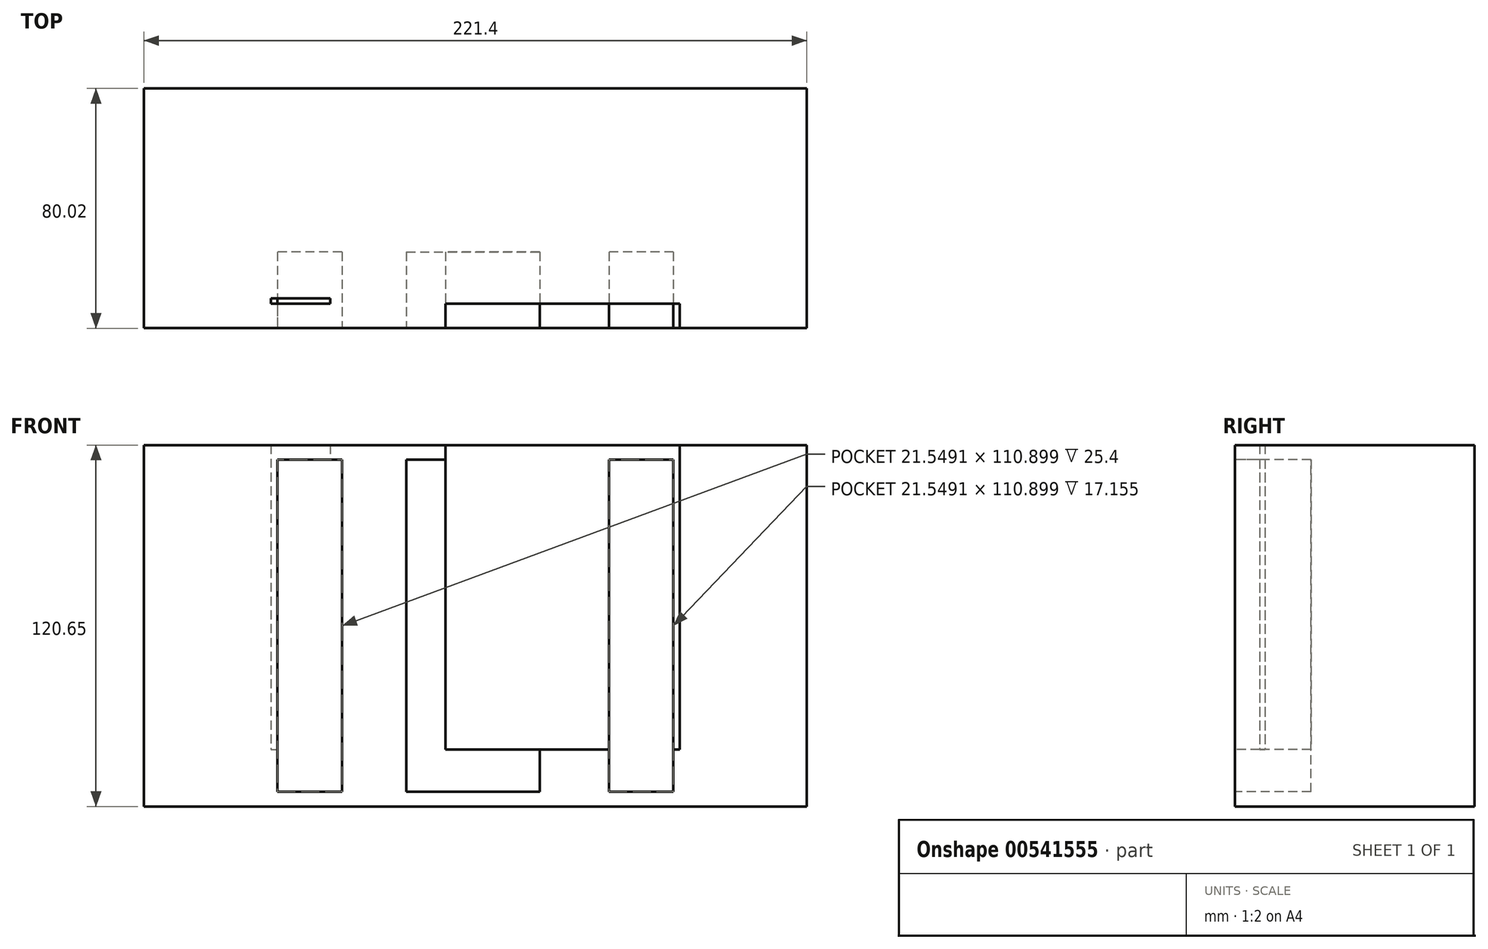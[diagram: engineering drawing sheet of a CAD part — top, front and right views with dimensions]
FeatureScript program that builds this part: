
annotation { "Feature Type Name" : "Feature", "Feature Type Description" : "" }
export const myFeature = defineFeature(function(context is Context, id is Id, definition is map)
    precondition{}
    {
        {
            var Q0;
            Q0=qCreatedBy(makeId("Top.planeOp"),FACE);
            var sketch = newSketch(context, id + "F0", { "sketchPlane" : qUnion([Q0])});
            skLineSegment(sketch, "E0.bottom", {"start": v(110.7, -40) * mm, "end": v(-110.7, -40) * mm});
            skLineSegment(sketch, "E0.top", {"start": v(110.7, 40) * mm, "end": v(-110.7, 40) * mm});
            skLineSegment(sketch, "E0.left", {"start": v(110.7, -40) * mm, "end": v(110.7, 40) * mm});
            skLineSegment(sketch, "E0.right", {"start": v(-110.7, -40) * mm, "end": v(-110.7, 40) * mm});
            skPoint(sketch, "E0.middle", {"position": v(0, 0) * mm});
            skSolve(sketch);
        }
        {
            var Q0;
            Q0=makeQuery(id+"F0.imprint","IMPRINT",FACE,{"disambiguationData":[TD([[makeQuery(id+"F0.imprint","IMPRINT",EDGE,{"derivedFrom":sQuery(id+"F0.wireOp",EDGE,"E0.bottom")}),-1.0]])]});
            extrude(context, id + "F1", {"entities" : qUnion([Q0]), "depth" : 19.05 * mm, "offsetDistance" : 25.4 * mm});
        }
        {
            var Q0;
            Q0=makeQuery(id+"F1.opExtrude","CAP_FACE",FACE,{"disambiguationData":[OSD([sQuery(id+"F0.wireOp",EDGE,"E0.bottom"),sQuery(id+"F0.wireOp",EDGE,"E0.top"),sQuery(id+"F0.wireOp",EDGE,"E0.left"),sQuery(id+"F0.wireOp",EDGE,"E0.right")])],"isStart":false});
            var sketch = newSketch(context, id + "F2", { "sketchPlane" : qUnion([Q0])});
            skLineSegment(sketch, "E1", {"start": v(-96.86, 40) * mm, "end": v(-96.86, -40) * mm});
            skLineSegment(sketch, "E2", {"start": v(-110.7, 40) * mm, "end": v(-110.7, -40) * mm});
            skLineSegment(sketch, "E3.MirrorCS", {"start": v(96.86, 40) * mm, "end": v(96.86, -40) * mm});
            skLineSegment(sketch, "E4.MirrorCS", {"start": v(110.7, 40) * mm, "end": v(110.7, -40) * mm});
            skLineSegment(sketch, "E5", {"start": v(-96.86, -40) * mm, "end": v(-110.7, -40) * mm});
            skLineSegment(sketch, "E6.MirrorCS", {"start": v(96.86, -40) * mm, "end": v(110.7, -40) * mm});
            skLineSegment(sketch, "E7", {"start": v(-110.7, 40) * mm, "end": v(-96.86, 40) * mm});
            skLineSegment(sketch, "E8", {"start": v(96.86, 40) * mm, "end": v(110.7, 40) * mm});
            skLineSegment(sketch, "E9.bottom", {"start": v(9.92, -40) * mm, "end": v(-9.92, -40) * mm});
            skLineSegment(sketch, "E9.top", {"start": v(9.92, -30) * mm, "end": v(-9.92, -30) * mm});
            skLineSegment(sketch, "E9.left", {"start": v(9.92, -40) * mm, "end": v(9.92, -30) * mm});
            skLineSegment(sketch, "E9.right", {"start": v(-9.92, -40) * mm, "end": v(-9.92, -30) * mm});
            skLineSegment(sketch, "E10", {"start": v(9.92, -40) * mm, "end": v(48.43, -40) * mm});
            skLineSegment(sketch, "E11.MirrorCS", {"start": v(48.43, -30) * mm, "end": v(68.28, -30) * mm});
            skLineSegment(sketch, "E12.MirrorCS", {"start": v(48.43, -40) * mm, "end": v(48.43, -30) * mm});
            skLineSegment(sketch, "E13.MirrorCS", {"start": v(68.28, -40) * mm, "end": v(68.28, -30) * mm});
            skLineSegment(sketch, "E14.MirrorCS", {"start": v(48.43, -40) * mm, "end": v(68.28, -40) * mm});
            skLineSegment(sketch, "E15.MirrorCS", {"start": v(-68.28, -30) * mm, "end": v(-48.43, -30) * mm});
            skLineSegment(sketch, "E16.MirrorCS", {"start": v(-48.43, -40) * mm, "end": v(-48.43, -30) * mm});
            skLineSegment(sketch, "E17.MirrorCS", {"start": v(-68.28, -40) * mm, "end": v(-68.28, -30) * mm});
            skLineSegment(sketch, "E18.MirrorCS", {"start": v(-68.28, -40) * mm, "end": v(-48.43, -40) * mm});
            skLineSegment(sketch, "E19", {"start": v(-96.86, 40) * mm, "end": v(96.86, 40) * mm});
            skLineSegment(sketch, "E20", {"start": v(-96.86, 31.76) * mm, "end": v(96.86, 31.76) * mm});
            skLineSegment(sketch, "E21", {"start": v(0, 0) * mm, "end": v(-60.31, 0) * mm});
            skLineSegment(sketch, "E22.MirrorCS", {"start": v(-96.86, -31.76) * mm, "end": v(96.86, -31.76) * mm});
            skLineSegment(sketch, "E23.MirrorCS", {"start": v(-96.86, -40) * mm, "end": v(96.86, -40) * mm});
            skSolve(sketch);
        }
        {
            var Q0;
            Q0=makeQuery(id+"F2.imprint","IMPRINT",FACE,{"disambiguationData":[TD([[makeQuery(id+"F2.imprint","IMPRINT",EDGE,{"derivedFrom":sQuery(id+"F2.wireOp",EDGE,"E2")}),-1.0]])]});
            var Q1;
            {var subQ0=sQuery(id+"F2.wireOp",EDGE,"E19");Q1=makeQuery(id+"F2.imprint","IMPRINT",FACE,{"disambiguationData":[TD([[makeQuery(id+"F2.imprint","IMPRINT",EDGE,{"derivedFrom":subQ0}),1.0]])]});}
            var Q2;
            Q2=makeQuery(id+"F2.imprint","IMPRINT",FACE,{"disambiguationData":[TD([[makeQuery(id+"F2.imprint","IMPRINT",EDGE,{"derivedFrom":sQuery(id+"F2.wireOp",EDGE,"E4.MirrorCS")}),1.0]])]});
            var Q3;
            {var subQ0=sQuery(id+"F2.wireOp",EDGE,"E23.MirrorCS");var subQ1=sQuery(id+"F2.wireOp",EDGE,"E9.left");var subQ2=makeQuery(id+"F2.imprint","INTERSECT",VERTEX,{"derivedFrom":[subQ1,subQ0]});Q3=makeQuery(id+"F2.imprint","IMPRINT",FACE,{"disambiguationData":[TD([[makeQuery(id+"F2.imprint","IMPRINT",EDGE,{"disambiguationData":[TD([[subQ2,-1.0]])],"derivedFrom":subQ1}),-1.0]])]});}
            var Q4;
            {var subQ0=sQuery(id+"F2.wireOp",EDGE,"E23.MirrorCS");var subQ1=sQuery(id+"F2.wireOp",EDGE,"E9.right");var subQ2=makeQuery(id+"F2.imprint","INTERSECT",VERTEX,{"derivedFrom":[subQ1,subQ0]});Q4=makeQuery(id+"F2.imprint","IMPRINT",FACE,{"disambiguationData":[TD([[makeQuery(id+"F2.imprint","IMPRINT",EDGE,{"disambiguationData":[TD([[subQ2,-1.0]])],"derivedFrom":subQ1}),1.0]])]});}
            var Q5;
            {var subQ0=sQuery(id+"F2.wireOp",EDGE,"E23.MirrorCS");var subQ5=sQuery(id+"F2.wireOp",EDGE,"E17.MirrorCS");var subQ6=makeQuery(id+"F2.imprint","INTERSECT",VERTEX,{"derivedFrom":[subQ5,subQ0]});Q5=makeQuery(id+"F2.imprint","IMPRINT",FACE,{"disambiguationData":[TD([[makeQuery(id+"F2.imprint","IMPRINT",EDGE,{"disambiguationData":[TD([[subQ6,-1.0]])],"derivedFrom":subQ5}),1.0]])]});}
            var Q6;
            {var subQ0=sQuery(id+"F2.wireOp",EDGE,"E23.MirrorCS");var subQ1=sQuery(id+"F2.wireOp",EDGE,"E16.MirrorCS");var subQ2=makeQuery(id+"F2.imprint","INTERSECT",VERTEX,{"derivedFrom":[subQ1,subQ0]});Q6=makeQuery(id+"F2.imprint","IMPRINT",FACE,{"disambiguationData":[TD([[makeQuery(id+"F2.imprint","IMPRINT",EDGE,{"disambiguationData":[TD([[subQ2,-1.0]])],"derivedFrom":subQ1}),1.0]])]});}
            var Q7;
            {var subQ0=sQuery(id+"F2.wireOp",EDGE,"E23.MirrorCS");var subQ1=sQuery(id+"F2.wireOp",EDGE,"E9.left");var subQ2=makeQuery(id+"F2.imprint","INTERSECT",VERTEX,{"derivedFrom":[subQ1,subQ0]});Q7=makeQuery(id+"F2.imprint","IMPRINT",FACE,{"disambiguationData":[TD([[makeQuery(id+"F2.imprint","IMPRINT",EDGE,{"disambiguationData":[TD([[subQ2,-1.0]])],"derivedFrom":subQ1}),1.0]])]});}
            var Q8;
            {var subQ0=sQuery(id+"F2.wireOp",EDGE,"E23.MirrorCS");var subQ1=sQuery(id+"F2.wireOp",EDGE,"E12.MirrorCS");var subQ2=makeQuery(id+"F2.imprint","INTERSECT",VERTEX,{"derivedFrom":[subQ1,subQ0]});Q8=makeQuery(id+"F2.imprint","IMPRINT",FACE,{"disambiguationData":[TD([[makeQuery(id+"F2.imprint","IMPRINT",EDGE,{"disambiguationData":[TD([[subQ2,-1.0]])],"derivedFrom":subQ1}),-1.0]])]});}
            var Q9;
            {var subQ0=sQuery(id+"F2.wireOp",EDGE,"E23.MirrorCS");var subQ5=sQuery(id+"F2.wireOp",EDGE,"E13.MirrorCS");var subQ6=makeQuery(id+"F2.imprint","INTERSECT",VERTEX,{"derivedFrom":[subQ5,subQ0]});Q9=makeQuery(id+"F2.imprint","IMPRINT",FACE,{"disambiguationData":[TD([[makeQuery(id+"F2.imprint","IMPRINT",EDGE,{"disambiguationData":[TD([[subQ6,-1.0]])],"derivedFrom":subQ5}),-1.0]])]});}
            extrude(context, id + "F3", {"entities" : qUnion([Q0, Q1, Q2, Q3, Q4, Q5, Q6, Q7, Q8, Q9]), "operationType" : NewBodyOperationType.ADD, "depth" : 101.6 * mm, "offsetDistance" : 25.4 * mm});
        }
        {
            var Q0;
            Q0=makeQuery(id+"F3.boolean.opBoolean","MERGE",FACE,{"derivedFrom":[makeQuery(id+"F1.opExtrude","SWEPT_FACE",FACE,{"disambiguationData":[OSD([sQuery(id+"F0.wireOp",EDGE,"E0.bottom")])]}),makeQuery(id+"F3.opExtrude","SWEPT_FACE",FACE,{"disambiguationData":[OSD([sQuery(id+"F2.wireOp",EDGE,"E5"),sQuery(id+"F2.wireOp",EDGE,"E6.MirrorCS"),sQuery(id+"F2.wireOp",EDGE,"E23.MirrorCS")])]})]});
            var sketch = newSketch(context, id + "F4", { "sketchPlane" : qUnion([Q0])});
            skLineSegment(sketch, "E24", {"start": v(-110.7, 120.65) * mm, "end": v(0, 120.65) * mm});
            skLineSegment(sketch, "E25", {"start": v(0, 120.65) * mm, "end": v(110.7, 120.65) * mm});
            skLineSegment(sketch, "E26", {"start": v(110.7, 120.65) * mm, "end": v(55.35, 120.65) * mm});
            skPoint(sketch, "E27.orphan", {"position": v(-55.35, 120.65) * mm});
            skLineSegment(sketch, "E28", {"start": v(-66.12, 115.78) * mm, "end": v(-44.58, 115.78) * mm});
            skLineSegment(sketch, "E29", {"start": v(-44.58, 4.88) * mm, "end": v(-66.12, 4.88) * mm});
            skLineSegment(sketch, "E30", {"start": v(-66.12, 4.88) * mm, "end": v(-66.12, 115.78) * mm});
            skLineSegment(sketch, "E31", {"start": v(-44.58, 115.78) * mm, "end": v(-44.58, 4.88) * mm});
            skPoint(sketch, "E32.start.orphan", {"position": v(-44.58, 0) * mm});
            skPoint(sketch, "E33.end.orphan", {"position": v(-44.58, 57.89) * mm});
            skPoint(sketch, "E33.start.orphan", {"position": v(-66.12, 57.89) * mm});
            skPoint(sketch, "E34.MirrorCS.end.orphan", {"position": v(66.12, 115.78) * mm});
            skLineSegment(sketch, "E35.MirrorCS", {"start": v(44.58, 115.78) * mm, "end": v(44.58, 4.88) * mm});
            skLineSegment(sketch, "E36.MirrorCS", {"start": v(66.12, 4.88) * mm, "end": v(66.12, 115.78) * mm});
            skLineSegment(sketch, "E37.MirrorCS", {"start": v(44.58, 4.88) * mm, "end": v(66.12, 4.88) * mm});
            skLineSegment(sketch, "E38.MirrorCS", {"start": v(66.12, 115.78) * mm, "end": v(44.58, 115.78) * mm});
            skLineSegment(sketch, "E39", {"start": v(-23.03, 4.88) * mm, "end": v(21.55, 4.88) * mm});
            skLineSegment(sketch, "E40", {"start": v(-23.03, 4.88) * mm, "end": v(-23.03, 115.78) * mm});
            skLineSegment(sketch, "E41", {"start": v(21.55, 4.88) * mm, "end": v(21.55, 115.78) * mm});
            skLineSegment(sketch, "E42", {"start": v(-23.03, 115.78) * mm, "end": v(21.55, 115.78) * mm});
            skSolve(sketch);
        }
        {
            var Q0;
            Q0=makeQuery(id+"F4.imprint","IMPRINT",FACE,{"disambiguationData":[TD([[makeQuery(id+"F4.imprint","IMPRINT",EDGE,{"derivedFrom":sQuery(id+"F4.wireOp",EDGE,"E28")}),-1.0]])]});
            var Q1;
            Q1=makeQuery(id+"F4.imprint","IMPRINT",FACE,{"disambiguationData":[TD([[makeQuery(id+"F4.imprint","IMPRINT",EDGE,{"derivedFrom":sQuery(id+"F4.wireOp",EDGE,"E39")}),1.0]])]});
            var Q2;
            Q2=makeQuery(id+"F4.imprint","IMPRINT",FACE,{"disambiguationData":[TD([[makeQuery(id+"F4.imprint","IMPRINT",EDGE,{"derivedFrom":sQuery(id+"F4.wireOp",EDGE,"E35.MirrorCS")}),1.0]])]});
            extrude(context, id + "F5", {"entities" : qUnion([Q0, Q1, Q2]), "operationType" : NewBodyOperationType.REMOVE, "oppositeDirection" : true, "depth" : 25.4 * mm, "offsetDistance" : 25.4 * mm});
        }
    });
